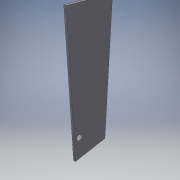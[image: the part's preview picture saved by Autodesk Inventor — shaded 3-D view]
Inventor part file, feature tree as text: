
AUTODESK INVENTOR PART (.ipt)
format: ipt  version: 2016 (Build 200138000, 138)  size: 98,304 bytes
history: native  units: in
note: dims shown in document units (in); Inventor stores cm internally (conversion verified against a paired STEP export)
features: extrude x2, sketch x2
ambient origin geometry x8: Origin, YZ Plane, XZ Plane, XY Plane, X Axis, Y Axis, Z Axis, Center Point
bodies: Solid1 (feature_tree)
feature tree (4):
  extrude  "Extrusion1"  Depth=18.0in
  extrude  "Extrusion2"  Depth=1.0in
  sketch  "Sketch1"  dims[d0=62.0in d1=18.0in]
  sketch  "Sketch2"  dims[d2=1.0in d3=0.0in d5=3.0in d8=2.8in d9=12.0in d12=1.0in d13=0.0in]
